# Revit family: CPS
name_source: partatom
category: Mechanical Equipment
units: mm (PartAtom-declared; Revit-internal decimal feet)

## family parameters
Always vertical = Yes
Cut with Voids When Loaded = No
Part Type = Normal
Room Calculation Point = No
Round Connector Dimension = Use Radius
Shared = No
Work Plane-Based = No

## types (33) — shared parameters
-.125 = -1/8"
-1.5 = -1 1/2"
0 = 0"
1.5 = 1 1/2"
CHECK = Yes
Manufacturer = Loren Cook Company
ONE EIGHTH = 1/8"
TA = 20"
TB = 3"
UNCHECK = No
URL = www.lorencook.com

## per-type parameters (varying)
- 135-CPS_CLASS_1: (C/2)-.25=8 9/16"; (C/2)-1.5=7 5/16"; -(A+.25)=-10 9/16"; A=10 5/16"; A+.25=10 9/16"; B=14 3/4"; C=17 5/8"; C/2=8 13/16"; C/8=2 15/16"; C/8*7=5 1/2"; CLASS=1"; CUT=2"; D=18"; E=26 11/16"; E-F=12 13/16"; F=13 7/8"; F-.125=13 3/4"; G=9 3/8"; G-V=1 3/8"; H=27"; J=13 1/2"; K=12"; L=13"; M=15 1/8"; Model=CPS_CLASS_1; N=12 1/8"; P=34 3/16"; P-D=16 3/16"; P-U=32 9/16"; Q=3"; R=1"; S=9/16"; S/2=9/32"; Stack Ht=88 1/8"; T=3/4"; Type Comments=Steel Flat Blade Centrifugal Blower Arrangement 10 Class 1; U=1 5/8"; U-.125=1 1/2"; V=8"; W=4"; W+1.5=5 1/2"; W+1.5+K+L=30 1/2"; W+M=19 1/8"; X=17 15/16"; Y=8 5/8"; Z=6"
- 150-CPS_CLASS_1: (C/2)-.25=9 5/16"; (C/2)-1.5=8 1/16"; -(A+.25)=-11 11/16"; A=11 7/16"; A+.25=11 11/16"; B=16 7/16"; C=19 1/8"; C/2=9 9/16"; C/8=3 3/16"; C/8*7=5 31/32"; CLASS=1"; CUT=2"; D=19 1/16"; E=29 9/16"; E-F=14 1/4"; F=15 5/16"; F-.125=15 3/16"; G=9 3/8"; G-V=1 3/8"; H=29 1/16"; J=14 5/8"; K=12"; L=14 1/8"; M=15 1/8"; Model=CPS_CLASS_1; N=13 1/4"; P=37 1/8"; P-D=18 1/16"; P-U=35 1/2"; Q=3"; R=1"; S=9/16"; S/2=9/32"; Stack Ht=85 5/8"; T=3/4"; Type Comments=Steel Flat Blade Centrifugal Blower Arrangement 10 Class 1; U=1 5/8"; U-.125=1 1/2"; V=8"; W=4"; W+1.5=5 1/2"; W+1.5+K+L=31 5/8"; W+M=19 1/8"; X=19 5/8"; Y=8 5/8"; Z=6 9/16"
- 165-CPS_CLASS_1: (C/2)-.25=10 11/32"; (C/2)-1.5=9 3/32"; -(A+.25)=-12 7/8"; A=12 5/8"; A+.25=12 7/8"; B=18 1/16"; C=21 3/16"; C/2=10 19/32"; C/8=3 17/32"; C/8*7=6 5/8"; CLASS=1"; CUT=2"; D=20 7/16"; E=32 1/16"; E-F=15 11/16"; F=16 3/8"; F-.125=16 1/4"; G=9 3/8"; G-V=1 3/8"; H=31 7/16"; J=15 13/16"; K=12"; L=15 5/16"; M=15 1/8"; Model=CPS_CLASS_1; N=14 7/16"; P=39 7/8"; P-D=19 7/16"; P-U=38 1/4"; Q=3"; R=1"; S=9/16"; S/2=9/32"; Stack Ht=83 3/16"; T=3/4"; Type Comments=Steel Flat Blade Centrifugal Blower Arrangement 10 Class 1; U=1 5/8"; U-.125=1 1/2"; V=8"; W=4"; W+1.5=5 1/2"; W+1.5+K+L=32 13/16"; W+M=19 1/8"; X=21 1/4"; Y=8 5/8"; Z=7 3/16"
- 180-CPS_CLASS_1: (C/2)-.25=11 3/32"; (C/2)-1.5=9 27/32"; -(A+.25)=-14"; A=13 3/4"; A+.25=14"; B=19 11/16"; C=22 11/16"; C/2=11 11/32"; C/8=3 25/32"; C/8*7=7 3/32"; CLASS=1"; CUT=2"; D=22 1/16"; E=34 3/4"; E-F=17 1/8"; F=17 5/8"; F-.125=17 1/2"; G=10 3/8"; G-V=1 3/8"; H=33 9/16"; J=16 15/16"; K=12"; L=16 7/16"; M=15 1/8"; Model=CPS_CLASS_1; N=15 9/16"; P=43 1/8"; P-D=21 1/16"; P-U=41 1/2"; Q=3"; R=1 3/16"; S=9/16"; S/2=9/32"; Stack Ht=80 5/16"; T=3/4"; Type Comments=Steel Flat Blade Centrifugal Blower Arrangement 10 Class 1; U=1 5/8"; U-.125=1 1/2"; V=9"; W=4"; W+1.5=5 1/2"; W+1.5+K+L=33 15/16"; W+M=19 1/8"; X=22 7/8"; Y=9 5/8"; Z=7 3/4"
- 195-CPS_CLASS_1: (C/2)-.25=11 27/32"; (C/2)-1.5=10 19/32"; -(A+.25)=-15 3/16"; A=14 15/16"; A+.25=15 3/16"; B=21 5/16"; C=24 3/16"; C/2=12 3/32"; C/8=4 1/32"; C/8*7=7 9/16"; CLASS=1"; CUT=2"; D=23 11/16"; E=36 5/16"; E-F=18 1/2"; F=17 13/16"; F-.125=17 11/16"; G=10 3/8"; G-V=1 3/8"; H=35 11/16"; J=18 3/16"; K=15"; L=17 5/8"; M=18 1/8"; Model=CPS_CLASS_1; N=16 3/4"; P=46 3/8"; P-D=22 11/16"; P-U=44 3/4"; Q=3"; R=1 3/16"; S=9/16"; S/2=9/32"; Stack Ht=78 1/2"; T=3/4"; Type Comments=Steel Flat Blade Centrifugal Blower Arrangement 10 Class 1; U=1 5/8"; U-.125=1 1/2"; V=9"; W=4"; W+1.5=5 1/2"; W+1.5+K+L=38 1/8"; W+M=22 1/8"; X=24 1/2"; Y=9 5/8"; Z=8 5/16"
- 210-CPS_CLASS_1: (C/2)-.25=12 23/32"; (C/2)-1.5=11 15/32"; -(A+.25)=-16 5/16"; A=16 1/16"; A+.25=16 5/16"; B=23"; C=25 15/16"; C/2=12 31/32"; C/8=4 5/16"; C/8*7=8 3/32"; CLASS=1"; CUT=2"; D=25 3/8"; E=39 15/16"; E-F=19 15/16"; F=20"; F-.125=19 7/8"; G=11 3/8"; G-V=1 3/8"; H=38 7/8"; J=19 5/16"; K=15"; L=18 3/4"; M=18 1/8"; Model=CPS_CLASS_1; N=17 7/8"; P=49 3/4"; P-D=24 3/8"; P-U=48 1/8"; Q=4"; R=1 7/16"; S=9/16"; S/2=9/32"; Stack Ht=74 5/8"; T=3/4"; Type Comments=Steel Flat Blade Centrifugal Blower Arrangement 10 Class 1; U=1 5/8"; U-.125=1 1/2"; V=10"; W=5"; W+1.5=6 1/2"; W+1.5+K+L=40 1/4"; W+M=23 1/8"; X=26 3/16"; Y=10 5/8"; Z=8 7/8"
- 225-CPS_CLASS_1: (C/2)-.25=13 15/32"; (C/2)-1.5=12 7/32"; -(A+.25)=-17 7/16"; A=17 3/16"; A+.25=17 7/16"; B=24 5/8"; C=27 7/16"; C/2=13 23/32"; C/8=4 9/16"; C/8*7=8 9/16"; CLASS=1"; CUT=2"; D=27"; E=42"; E-F=21 3/8"; F=20 5/8"; F-.125=20 1/2"; G=11 7/8"; G-V=1 3/8"; H=41"; J=20 7/16"; K=15"; L=19 7/8"; M=18 1/8"; Model=CPS_CLASS_1; N=19"; P=53"; P-D=26"; P-U=51 3/8"; Q=4"; R=1 7/16"; S=9/16"; S/2=9/32"; Stack Ht=72 3/8"; T=3/4"; Type Comments=Steel Flat Blade Centrifugal Blower Arrangement 10 Class 1; U=1 5/8"; U-.125=1 1/2"; V=10 1/2"; W=5"; W+1.5=6 1/2"; W+1.5+K+L=41 3/8"; W+M=23 1/8"; X=27 13/16"; Y=11 1/8"; Z=9 7/16"
- 245-CPS_CLASS_1: (C/2)-.25=14 15/32"; (C/2)-1.5=13 7/32"; -(A+.25)=-19"; A=18 3/4"; A+.25=19"; B=26 13/16"; C=29 7/16"; C/2=14 23/32"; C/8=4 29/32"; C/8*7=9 3/16"; CLASS=1"; CUT=2"; D=29 5/8"; E=45 1/16"; E-F=23 5/16"; F=21 3/4"; F-.125=21 5/8"; G=13 3/8"; G-V=1 7/8"; H=44 5/8"; J=23"; K=15"; L=21 11/16"; M=18 1/8"; Model=CPS_CLASS_1; N=21 1/16"; P=58 1/4"; P-D=28 5/8"; P-U=56 1/8"; Q=4"; R=1 11/16"; S=11/16"; S/2=11/32"; Stack Ht=68 5/8"; T=1"; Type Comments=Steel Flat Blade Centrifugal Blower Arrangement 10 Class 1; U=2 1/8"; U-.125=2"; V=11 1/2"; W=5"; W+1.5=6 1/2"; W+1.5+K+L=43 3/16"; W+M=23 1/8"; X=31"; Y=12 3/8"; Z=10 1/2"
- 270-CPS_CLASS_1: (C/2)-.25=15 23/32"; (C/2)-1.5=14 15/32"; -(A+.25)=-20 7/8"; A=20 5/8"; A+.25=20 7/8"; B=29 9/16"; C=31 15/16"; C/2=15 31/32"; C/8=5 5/16"; C/8*7=9 31/32"; CLASS=1"; CUT=2 1/4"; D=32 3/8"; E=49 1/16"; E-F=25 11/16"; F=23 3/8"; F-.125=23 1/4"; G=14 3/8"; G-V=1 7/8"; H=48 7/8"; J=24 7/8"; K=18"; L=23 9/16"; M=21 1/8"; Model=CPS_CLASS_1; N=22 15/16"; P=63 3/4"; P-D=31 3/8"; P-U=61 5/8"; Q=4"; R=1 11/16"; S=11/16"; S/2=11/32"; Stack Ht=64 1/4"; T=1"; Type Comments=Steel Flat Blade Centrifugal Blower Arrangement 10 Class 1; U=2 1/8"; U-.125=2"; V=12 1/2"; W=5"; W+1.5=6 1/2"; W+1.5+K+L=48 1/16"; W+M=26 1/8"; X=33 3/4"; Y=13 3/8"; Z=11 7/16"
- 300-CPS_CLASS_1: (C/2)-.25=17 7/32"; (C/2)-1.5=15 31/32"; -(A+.25)=-23 3/16"; A=22 15/16"; A+.25=23 3/16"; B=32 13/16"; C=34 15/16"; C/2=17 15/32"; C/8=5 13/16"; C/8*7=10 29/32"; CLASS=1"; CUT=2 1/2"; D=35 5/8"; E=54 3/8"; E-F=28 1/2"; F=25 7/8"; F-.125=25 3/4"; G=15 5/16"; G-V=1 13/16"; H=53 5/8"; J=27 3/16"; K=18"; L=26"; M=21 3/16"; Model=CPS_CLASS_1; N=25 5/16"; P=71 1/4"; P-D=35 5/8"; P-U=69 1/8"; Q=4"; R=1 15/16"; S=11/16"; S/2=11/32"; Stack Ht=58 1/2"; T=1"; Type Comments=Steel Flat Blade Centrifugal Blower Arrangement 10 Class 1; U=2 1/8"; U-.125=2"; V=13 1/2"; W=5"; W+1.5=6 1/2"; W+1.5+K+L=50 1/2"; W+M=26 3/16"; X=37"; Y=14 5/16"; Z=12 5/8"
- 330-CPS_CLASS_1: (C/2)-.25=18 23/32"; (C/2)-1.5=17 15/32"; -(A+.25)=-25 1/2"; A=25 1/4"; A+.25=25 1/2"; B=36 1/8"; C=37 15/16"; C/2=18 31/32"; C/8=6 5/16"; C/8*7=11 27/32"; CLASS=1"; CUT=2 3/4"; D=38 7/8"; E=59 13/16"; E-F=31 3/8"; F=28 7/16"; F-.125=28 5/16"; G=16 13/16"; G-V=1 13/16"; H=58 3/8"; J=29 7/16"; K=18"; L=28 5/16"; M=21 3/16"; Model=CPS_CLASS_1; N=27 5/8"; P=76 3/4"; P-D=37 7/8"; P-U=74 5/8"; Q=4"; R=1 15/16"; S=13/16"; S/2=13/32"; Stack Ht=52 11/16"; T=1"; Type Comments=Steel Flat Blade Centrifugal Blower Arrangement 10 Class 1; U=2 1/8"; U-.125=2"; V=15"; W=5"; W+1.5=6 1/2"; W+1.5+K+L=52 13/16"; W+M=26 3/16"; X=40 5/16"; Y=15 13/16"; Z=13 3/4"
- 365-CPS_CLASS_1: (C/2)-.25=20 15/32"; (C/2)-1.5=19 7/32"; -(A+.25)=-28 1/8"; A=27 7/8"; A+.25=28 1/8"; B=39 15/16"; C=41 7/16"; C/2=20 23/32"; C/8=6 29/32"; C/8*7=12 15/16"; CLASS=1"; CUT=3"; D=42 3/4"; E=66 1/8"; E-F=34 11/16"; F=31 7/16"; F-.125=31 5/16"; G=17 13/16"; G-V=1 13/16"; H=64 1/4"; J=32 1/16"; K=21"; L=30 15/16"; M=24 3/16"; Model=CPS_CLASS_1; N=30 1/4"; P=84 1/2"; P-D=41 3/4"; P-U=82 3/8"; Q=5"; R=2 3/16"; S=13/16"; S/2=13/32"; Stack Ht=45 13/16"; T=1"; Type Comments=Steel Flat Blade Centrifugal Blower Arrangement 10 Class 1; U=2 1/8"; U-.125=2"; V=16"; W=6"; W+1.5=7 1/2"; W+1.5+K+L=59 7/16"; W+M=30 3/16"; X=44 3/16"; Y=16 13/16"; Z=15 1/16"
- 402-CPS_CLASS_1: (C/2)-.25=22 11/32"; (C/2)-1.5=21 3/32"; -(A+.25)=-31"; A=30 3/4"; A+.25=31"; B=44 1/16"; C=45 3/16"; C/2=22 19/32"; C/8=7 17/32"; C/8*7=14 1/8"; CLASS=1"; CUT=3 1/4"; D=46 3/4"; E=72 15/16"; E-F=38 1/4"; F=34 11/16"; F-.125=34 9/16"; G=19 13/16"; G-V=1 13/16"; H=70 1/4"; J=34 15/16"; K=21"; L=34 5/16"; M=24 3/16"; Model=CPS_CLASS_1; N=34 1/8"; P=92 1/2"; P-D=45 3/4"; P-U=90 3/8"; Q=5"; R=2 3/16"; S=13/16"; S/2=13/32"; Stack Ht=38 9/16"; T=1"; Type Comments=Steel Flat Blade Centrifugal Blower Arrangement 10 Class 1; U=2 1/8"; U-.125=2"; V=18"; W=6"; W+1.5=7 1/2"; W+1.5+K+L=62 13/16"; W+M=30 3/16"; X=48 5/16"; Y=18 13/16"; Z=17"
- 445-CPS_CLASS_1: (C/2)-.25=24 15/32"; (C/2)-1.5=23 7/32"; -(A+.25)=-34 1/4"; A=34"; A+.25=34 1/4"; B=48 11/16"; C=49 7/16"; C/2=24 23/32"; C/8=8 1/4"; C/8*7=15 7/16"; CLASS=1"; CUT=3 1/2"; D=51 3/8"; E=80 9/16"; E-F=42 1/4"; F=38 5/16"; F-.125=38 3/16"; G=21 13/16"; G-V=1 13/16"; H=76 7/8"; J=38 3/16"; K=25"; L=37 9/16"; M=28 3/16"; Model=CPS_CLASS_1; N=37 3/8"; P=101 3/4"; P-D=50 3/8"; P-U=99 5/8"; Q=5"; R=2 7/16"; S=13/16"; S/2=13/32"; Stack Ht=30 5/16"; T=1"; Type Comments=Steel Flat Blade Centrifugal Blower Arrangement 10 Class 1; U=2 1/8"; U-.125=2"; V=20"; W=6"; W+1.5=7 1/2"; W+1.5+K+L=70 1/16"; W+M=34 3/16"; X=52 15/16"; Y=20 13/16"; Z=18 5/8"
- 490-CPS_CLASS_1: (C/2)-.25=27 1/4"; (C/2)-1.5=26"; -(A+.25)=-37 7/16"; A=37 3/16"; A+.25=37 7/16"; B=53 5/8"; C=55"; C/2=27 1/2"; C/8=9 5/32"; C/8*7=17 3/16"; CLASS=1"; CUT=4"; D=56 1/4"; E=88 3/4"; E-F=46 9/16"; F=42 3/16"; F-.125=42 1/16"; G=23 13/16"; G-V=1 13/16"; H=84 1/4"; J=41 5/8"; K=25"; L=41"; M=28 3/16"; Model=CPS_CLASS_1; N=40 3/16"; P=111 1/2"; P-D=55 1/4"; P-U=109 3/8"; Q=5"; R=2 7/16"; S=13/16"; S/2=13/32"; Stack Ht=21 9/16"; T=1"; Type Comments=Steel Flat Blade Centrifugal Blower Arrangement 10 Class 1; U=2 1/8"; U-.125=2"; V=22"; W=6"; W+1.5=7 1/2"; W+1.5+K+L=73 1/2"; W+M=34 3/16"; X=57 7/8"; Y=22 13/16"; Z=20 3/8"
- 120-CPS_CLASS_1: (C/2)-.25=7 13/16"; (C/2)-1.5=6 9/16"; -(A+.25)=-9 7/16"; A=9 3/16"; A+.25=9 7/16"; B=13 1/8"; C=16 1/8"; C/2=8 1/16"; C/8=2 11/16"; C/8*7=5 1/32"; CLASS=1"; CUT=2 1/2"; D=18"; E=24 13/16"; E-F=11 7/16"; F=13 3/8"; F-.125=13 1/4"; G=9 3/8"; G-V=1 3/8"; H=26 1/4"; J=12 3/8"; K=10"; L=11 7/8"; M=13 1/8"; Model=CPS_CLASS_1; N=11"; P=32 9/16"; P-D=14 9/16"; P-U=30 15/16"; Q=3"; R=1"; S=9/16"; S/2=9/32"; Stack Ht=88 5/8"; T=3/4"; Type Comments=Steel Flat Blade Centrifugal Blower Arrangement 10 Class 1; U=1 5/8"; U-.125=1 1/2"; V=8"; W=4"; W+1.5=5 1/2"; W+1.5+K+L=27 3/8"; W+M=17 1/8"; X=16 5/16"; Y=8 5/8"; Z=5 7/16"
- 100-CPS_CLASS_1: (C/2)-.25=6 13/16"; (C/2)-1.5=5 9/16"; -(A+.25)=-7 13/16"; A=7 9/16"; A+.25=7 13/16"; B=10 15/16"; C=14 1/8"; C/2=7 1/16"; C/8=2 11/32"; C/8*7=4 13/32"; CLASS=1"; CUT=3 1/2"; D=18"; E=22 1/4"; E-F=9 1/2"; F=12 3/4"; F-.125=12 5/8"; G=9 3/8"; G-V=1 3/8"; H=25 1/4"; J=10 3/4"; K=10"; L=10 1/4"; M=13 1/8"; Model=CPS_CLASS_1; N=9 3/8"; P=30 3/8"; P-D=12 3/8"; P-U=28 3/4"; Q=3"; R=1"; S=9/16"; S/2=9/32"; Stack Ht=89 1/4"; T=3/4"; Type Comments=Steel Flat Blade Centrifugal Blower Arrangement 10 Class 1; U=1 5/8"; U-.125=1 1/2"; V=8"; W=4"; W+1.5=5 1/2"; W+1.5+K+L=25 3/4"; W+M=17 1/8"; X=14 1/16"; Y=8 5/8"; Z=4 5/8"
- 120-CPS_CLASS_2: (C/2)-.25=7 13/16"; (C/2)-1.5=6 9/16"; -(A+.25)=-9 7/16"; A=9 3/16"; A+.25=9 7/16"; B=13 1/8"; C=16 1/8"; C/2=8 1/16"; C/8=2 11/16"; C/8*7=5 1/32"; CLASS=2"; CUT=2 1/2"; D=22"; E=24 7/8"; E-F=11 1/2"; F=13 3/8"; F-.125=13 1/4"; G=10 3/8"; G-V=1 3/8"; H=30 1/4"; J=12 3/8"; K=18"; L=12 5/16"; M=21 1/8"; Model=CPS_CLASS_2; N=11 1/4"; P=36 5/8"; P-D=14 5/8"; P-U=35"; Q=3"; R=1 7/16"; S=9/16"; S/2=9/32"; Stack Ht=84 5/8"; T=3/4"; Type Comments=Steel Flat Blade Centrifugal Blower Arrangement 10 Class 2; U=1 5/8"; U-.125=1 1/2"; V=9"; W=4"; W+1.5=5 1/2"; W+1.5+K+L=35 13/16"; W+M=25 1/8"; X=16 5/16"; Y=9 5/8"; Z=5 9/16"
- 135-CPS_CLASS_2: (C/2)-.25=8 9/16"; (C/2)-1.5=7 5/16"; -(A+.25)=-10 9/16"; A=10 5/16"; A+.25=10 9/16"; B=14 5/8"; C=17 5/8"; C/2=8 13/16"; C/8=2 15/16"; C/8*7=5 1/2"; CLASS=2"; CUT=2"; D=22"; E=26 3/4"; E-F=12 7/8"; F=13 7/8"; F-.125=13 3/4"; G=10 3/8"; G-V=1 3/8"; H=31"; J=13 1/2"; K=18"; L=13 7/16"; M=21 1/8"; Model=CPS_CLASS_2; N=12 3/8"; P=38 1/4"; P-D=16 1/4"; P-U=36 5/8"; Q=3"; R=1 7/16"; S=9/16"; S/2=9/32"; Stack Ht=84 1/8"; T=3/4"; Type Comments=Steel Flat Blade Centrifugal Blower Arrangement 10 Class 2; U=1 5/8"; U-.125=1 1/2"; V=9"; W=4"; W+1.5=5 1/2"; W+1.5+K+L=36 15/16"; W+M=25 1/8"; X=17 15/16"; Y=9 5/8"; Z=6 1/8"
- 150-CPS_CLASS_2: (C/2)-.25=9 5/16"; (C/2)-1.5=8 1/16"; -(A+.25)=-11 11/16"; A=11 7/16"; A+.25=11 11/16"; B=16 7/16"; C=19 1/8"; C/2=9 9/16"; C/8=3 3/16"; C/8*7=5 31/32"; CLASS=2"; CUT=2"; D=22"; E=29 5/8"; E-F=14 5/16"; F=15 5/16"; F-.125=15 3/16"; G=10 7/8"; G-V=1 3/8"; H=32"; J=14 5/8"; K=18"; L=15 15/32"; M=21 1/8"; Model=CPS_CLASS_2; N=13 1/2"; P=39 7/8"; P-D=17 7/8"; P-U=38 1/4"; Q=3"; R=1 7/16"; S=9/16"; S/2=9/32"; Stack Ht=82 11/16"; T=3/4"; Type Comments=Steel Flat Blade Centrifugal Blower Arrangement 10 Class 2; U=1 5/8"; U-.125=1 1/2"; V=9 1/2"; W=4"; W+1.5=5 1/2"; W+1.5+K+L=38 31/32"; W+M=25 1/8"; X=19 5/8"; Y=10 1/8"; Z=6 11/16"
- 165-CPS_CLASS_2: (C/2)-.25=10 11/32"; (C/2)-1.5=9 3/32"; -(A+.25)=-12 7/8"; A=12 5/8"; A+.25=12 7/8"; B=18 1/16"; C=21 3/16"; C/2=10 19/32"; C/8=3 17/32"; C/8*7=6 5/8"; CLASS=2"; CUT=2"; D=24"; E=32 1/8"; E-F=15 3/4"; F=16 3/8"; F-.125=16 1/4"; G=13"; G-V=1 3/4"; H=35"; J=15 13/16"; K=22 1/8"; L=16 1/8"; M=25 1/4"; Model=CPS_CLASS_2; N=15 1/16"; P=43 1/2"; P-D=19 1/2"; P-U=41 7/8"; Q=3"; R=1 7/16"; S=9/16"; S/2=9/32"; Stack Ht=79 5/8"; T=3/4"; Type Comments=Steel Flat Blade Centrifugal Blower Arrangement 10 Class 2; U=1 5/8"; U-.125=1 1/2"; V=11 1/4"; W=4"; W+1.5=5 1/2"; W+1.5+K+L=43 3/4"; W+M=29 1/4"; X=21 1/4"; Y=12 1/4"; Z=7 5/8"
- 180-CPS_CLASS_2: (C/2)-.25=11 3/32"; (C/2)-1.5=9 27/32"; -(A+.25)=-14"; A=13 3/4"; A+.25=14"; B=19 11/16"; C=22 11/16"; C/2=11 11/32"; C/8=3 25/32"; C/8*7=7 3/32"; CLASS=2"; CUT=2"; D=24"; E=34 13/16"; E-F=17 3/16"; F=17 5/8"; F-.125=17 1/2"; G=13"; G-V=1 3/4"; H=35 1/2"; J=16 15/16"; K=22 1/8"; L=17 1/4"; M=25 1/4"; Model=CPS_CLASS_2; N=16 3/16"; P=45 1/8"; P-D=21 1/8"; P-U=43 1/2"; Q=3"; R=1 11/16"; S=9/16"; S/2=9/32"; Stack Ht=78 3/8"; T=3/4"; Type Comments=Steel Flat Blade Centrifugal Blower Arrangement 10 Class 2; U=1 5/8"; U-.125=1 1/2"; V=11 1/4"; W=4"; W+1.5=5 1/2"; W+1.5+K+L=44 7/8"; W+M=29 1/4"; X=22 7/8"; Y=12 1/4"; Z=8 3/16"
- 195-CPS_CLASS_2: (C/2)-.25=11 27/32"; (C/2)-1.5=10 19/32"; -(A+.25)=-15 3/16"; A=14 15/16"; A+.25=15 3/16"; B=21 5/16"; C=24 3/16"; C/2=12 3/32"; C/8=4 1/32"; C/8*7=7 9/16"; CLASS=2"; CUT=2"; D=24 1/4"; E=36 3/8"; E-F=18 9/16"; F=17 13/16"; F-.125=17 11/16"; G=13 3/4"; G-V=1 3/4"; H=36 1/4"; J=18 3/16"; K=22 1/8"; L=18 1/2"; M=25 1/4"; Model=CPS_CLASS_2; N=17 3/8"; P=47"; P-D=22 3/4"; P-U=45 3/8"; Q=3"; R=1 11/16"; S=9/16"; S/2=9/32"; Stack Ht=77 15/16"; T=3/4"; Type Comments=Steel Flat Blade Centrifugal Blower Arrangement 10 Class 2; U=1 5/8"; U-.125=1 1/2"; V=12"; W=4"; W+1.5=5 1/2"; W+1.5+K+L=46 1/8"; W+M=29 1/4"; X=24 1/2"; Y=13"; Z=8 13/16"
- 210-CPS_CLASS_2: (C/2)-.25=12 23/32"; (C/2)-1.5=11 15/32"; -(A+.25)=-16 5/16"; A=16 1/16"; A+.25=16 5/16"; B=23"; C=25 15/16"; C/2=12 31/32"; C/8=4 5/16"; C/8*7=8 3/32"; CLASS=2"; CUT=2"; D=25 3/8"; E=40"; E-F=20"; F=20"; F-.125=19 7/8"; G=13 3/4"; G-V=1 3/4"; H=39"; J=19 5/16"; K=22 1/8"; L=19 5/8"; M=25 1/4"; Model=CPS_CLASS_2; N=18 1/2"; P=49 13/16"; P-D=24 7/16"; P-U=48 3/16"; Q=4"; R=1 11/16"; S=9/16"; S/2=9/32"; Stack Ht=74 5/8"; T=3/4"; Type Comments=Steel Flat Blade Centrifugal Blower Arrangement 10 Class 2; U=1 5/8"; U-.125=1 1/2"; V=12"; W=5"; W+1.5=6 1/2"; W+1.5+K+L=48 1/4"; W+M=30 1/4"; X=26 3/16"; Y=13"; Z=9 3/8"
- 225-CPS_CLASS_2: (C/2)-.25=13 15/32"; (C/2)-1.5=12 7/32"; -(A+.25)=-17 7/16"; A=17 3/16"; A+.25=17 7/16"; B=24 5/8"; C=27 7/16"; C/2=13 23/32"; C/8=4 9/16"; C/8*7=8 9/16"; CLASS=2"; CUT=2"; D=27"; E=42 1/16"; E-F=21 7/16"; F=20 5/8"; F-.125=20 1/2"; G=13 7/8"; G-V=1 13/16"; H=41"; J=20 7/16"; K=22 1/8"; L=20 7/8"; M=25 1/4"; Model=CPS_CLASS_2; N=19 3/4"; P=53 3/16"; P-D=26 3/16"; P-U=51 9/16"; Q=4"; R=1 11/16"; S=9/16"; S/2=9/32"; Stack Ht=72 3/8"; T=3/4"; Type Comments=Steel Flat Blade Centrifugal Blower Arrangement 10 Class 2; U=1 5/8"; U-.125=1 1/2"; V=12 1/16"; W=5"; W+1.5=6 1/2"; W+1.5+K+L=49 1/2"; W+M=30 1/4"; X=27 13/16"; Y=13 1/8"; Z=10 1/16"
- 245-CPS_CLASS_2: (C/2)-.25=14 15/32"; (C/2)-1.5=13 7/32"; -(A+.25)=-19"; A=18 3/4"; A+.25=19"; B=26 13/16"; C=29 7/16"; C/2=14 23/32"; C/8=4 29/32"; C/8*7=9 3/16"; CLASS=2"; CUT=2"; D=29 5/8"; E=45 1/8"; E-F=23 3/8"; F=21 3/4"; F-.125=21 5/8"; G=14 15/16"; G-V=1 13/16"; H=44 5/8"; J=23"; K=24 1/8"; L=22 5/16"; M=27 5/16"; Model=CPS_CLASS_2; N=21 5/16"; P=58 5/16"; P-D=28 11/16"; P-U=56 3/16"; Q=4"; R=1 15/16"; S=11/16"; S/2=11/32"; Stack Ht=68 5/8"; T=1"; Type Comments=Steel Flat Blade Centrifugal Blower Arrangement 10 Class 2; U=2 1/8"; U-.125=2"; V=13 1/8"; W=5"; W+1.5=6 1/2"; W+1.5+K+L=52 15/16"; W+M=32 5/16"; X=31"; Y=13 15/16"; Z=10 5/8"
- 270-CPS_CLASS_2: (C/2)-.25=15 23/32"; (C/2)-1.5=14 15/32"; -(A+.25)=-20 7/8"; A=20 5/8"; A+.25=20 7/8"; B=29 9/16"; C=31 15/16"; C/2=15 31/32"; C/8=5 5/16"; C/8*7=9 31/32"; CLASS=2"; CUT=2 1/4"; D=32 3/8"; E=49 1/8"; E-F=25 3/4"; F=23 3/8"; F-.125=23 1/4"; G=15 7/16"; G-V=2 5/16"; H=48 7/8"; J=24 7/8"; K=24 1/8"; L=24 11/16"; M=27 5/16"; Model=CPS_CLASS_2; N=23 11/16"; P=63 13/16"; P-D=31 7/16"; P-U=61 11/16"; Q=4"; R=1 15/16"; S=11/16"; S/2=11/32"; Stack Ht=64 1/4"; T=1"; Type Comments=Steel Flat Blade Centrifugal Blower Arrangement 10 Class 2; U=2 1/8"; U-.125=2"; V=13 1/8"; W=5"; W+1.5=6 1/2"; W+1.5+K+L=55 5/16"; W+M=32 5/16"; X=33 3/4"; Y=14 7/16"; Z=12 1/16"
- 300-CPS_CLASS_2: (C/2)-.25=17 7/32"; (C/2)-1.5=15 31/32"; -(A+.25)=-23 3/16"; A=22 15/16"; A+.25=23 3/16"; B=32 13/16"; C=34 15/16"; C/2=17 15/32"; C/8=5 13/16"; C/8*7=10 29/32"; CLASS=2"; CUT=2 1/2"; D=35 5/8"; E=54 1/2"; E-F=28 5/8"; F=25 7/8"; F-.125=25 3/4"; G=16 1/16"; G-V=2 3/8"; H=53 5/8"; J=27 3/16"; K=26"; L=27 3/16"; M=29 3/16"; Model=CPS_CLASS_2; N=26 3/16"; P=70 3/8"; P-D=34 3/4"; P-U=68 1/4"; Q=4"; R=2 3/16"; S=11/16"; S/2=11/32"; Stack Ht=58 1/2"; T=1"; Type Comments=Steel Flat Blade Centrifugal Blower Arrangement 10 Class 2; U=2 1/8"; U-.125=2"; V=13 11/16"; W=5"; W+1.5=6 1/2"; W+1.5+K+L=59 11/16"; W+M=34 3/16"; X=37"; Y=15 1/16"; Z=13 5/16"
- 330-CPS_CLASS_2: (C/2)-.25=18 23/32"; (C/2)-1.5=17 15/32"; -(A+.25)=-25 1/2"; A=25 1/4"; A+.25=25 1/2"; B=36 1/8"; C=37 15/16"; C/2=18 31/32"; C/8=6 5/16"; C/8*7=11 27/32"; CLASS=2"; CUT=2 3/4"; D=38 7/8"; E=59 15/16"; E-F=31 1/2"; F=28 7/16"; F-.125=28 5/16"; G=17 5/8"; G-V=2 3/8"; H=58 3/8"; J=29 7/16"; K=26"; L=29 9/16"; M=29 3/16"; Model=CPS_CLASS_2; N=28 9/16"; P=76 7/8"; P-D=38"; P-U=74 3/4"; Q=4"; R=2 3/16"; S=13/16"; S/2=13/32"; Stack Ht=52 11/16"; T=1"; Type Comments=Steel Flat Blade Centrifugal Blower Arrangement 10 Class 2; U=2 1/8"; U-.125=2"; V=15 1/4"; W=5"; W+1.5=6 1/2"; W+1.5+K+L=62 1/16"; W+M=34 3/16"; X=40 5/16"; Y=16 5/8"; Z=14 9/16"
- 365-CPS_CLASS_2: (C/2)-.25=20 15/32"; (C/2)-1.5=19 7/32"; -(A+.25)=-28 1/8"; A=27 7/8"; A+.25=28 1/8"; B=39 15/16"; C=41 7/16"; C/2=20 23/32"; C/8=6 29/32"; C/8*7=12 15/16"; CLASS=2"; CUT=3"; D=42 3/4"; E=66 3/16"; E-F=34 3/4"; F=31 7/16"; F-.125=31 5/16"; G=18 13/16"; G-V=2 5/8"; H=64 1/4"; J=32 1/16"; K=26"; L=32 9/16"; M=29 1/4"; Model=CPS_CLASS_2; N=31 7/16"; P=84 1/2"; P-D=41 3/4"; P-U=82 3/8"; Q=5"; R=2 7/16"; S=13/16"; S/2=13/32"; Stack Ht=45 13/16"; T=1"; Type Comments=Steel Flat Blade Centrifugal Blower Arrangement 10 Class 2; U=2 1/8"; U-.125=2"; V=16 3/16"; W=6"; W+1.5=7 1/2"; W+1.5+K+L=66 1/16"; W+M=35 1/4"; X=44 3/16"; Y=17 13/16"; Z=16 1/8"
- 60-CPS_CLASS_1: (C/2)-.25=6 13/16"; (C/2)-1.5=5 9/16"; -(A+.25)=-7 13/16"; A=7 9/16"; A+.25=7 13/16"; B=10 15/16"; C=14 1/8"; C/2=7 1/16"; C/8=2 11/32"; C/8*7=4 13/32"; CLASS=1"; CUT=3 1/2"; D=18"; E=22 1/4"; E-F=9 1/2"; F=12 3/4"; F-.125=12 5/8"; G=9 3/8"; G-V=1 3/8"; H=25 1/4"; J=10 3/4"; K=10"; L=10 1/4"; M=13 1/8"; Model=CPS_CLASS_1; N=9 3/8"; P=30 3/8"; P-D=12 3/8"; P-U=28 3/4"; Q=3"; R=1"; S=9/16"; S/2=9/32"; Stack Ht=89 1/4"; T=3/4"; Type Comments=Steel Flat Blade Centrifugal Blower Arrangement 10 Class 1; U=1 5/8"; U-.125=1 1/2"; V=8"; W=4"; W+1.5=5 1/2"; W+1.5+K+L=25 3/4"; W+M=17 1/8"; X=14 1/16"; Y=8 5/8"; Z=4 5/8"
- 70-CPS_CLASS_1: (C/2)-.25=6 13/16"; (C/2)-1.5=5 9/16"; -(A+.25)=-7 13/16"; A=7 9/16"; A+.25=7 13/16"; B=10 15/16"; C=14 1/8"; C/2=7 1/16"; C/8=2 11/32"; C/8*7=4 13/32"; CLASS=1"; CUT=3 1/2"; D=18"; E=22 1/4"; E-F=9 1/2"; F=12 3/4"; F-.125=12 5/8"; G=9 3/8"; G-V=1 3/8"; H=25 1/4"; J=10 3/4"; K=10"; L=10 1/4"; M=13 1/8"; Model=CPS_CLASS_1; N=9 3/8"; P=30 3/8"; P-D=12 3/8"; P-U=28 3/4"; Q=3"; R=1"; S=9/16"; S/2=9/32"; Stack Ht=89 1/4"; T=3/4"; Type Comments=Steel Flat Blade Centrifugal Blower Arrangement 10 Class 1; U=1 5/8"; U-.125=1 1/2"; V=8"; W=4"; W+1.5=5 1/2"; W+1.5+K+L=25 3/4"; W+M=17 1/8"; X=14 1/16"; Y=8 5/8"; Z=4 5/8"
- 80-CPS_CLASS_1: (C/2)-.25=6 13/16"; (C/2)-1.5=5 9/16"; -(A+.25)=-7 13/16"; A=7 9/16"; A+.25=7 13/16"; B=10 15/16"; C=14 1/8"; C/2=7 1/16"; C/8=2 11/32"; C/8*7=4 13/32"; CLASS=1"; CUT=3 1/2"; D=18"; E=22 1/4"; E-F=9 1/2"; F=12 3/4"; F-.125=12 5/8"; G=9 3/8"; G-V=1 3/8"; H=25 1/4"; J=10 3/4"; K=10"; L=10 1/4"; M=13 1/8"; Model=CPS_CLASS_1; N=9 3/8"; P=30 3/8"; P-D=12 3/8"; P-U=28 3/4"; Q=3"; R=1"; S=9/16"; S/2=9/32"; Stack Ht=89 1/4"; T=3/4"; Type Comments=Steel Flat Blade Centrifugal Blower Arrangement 10 Class 1; U=1 5/8"; U-.125=1 1/2"; V=8"; W=4"; W+1.5=5 1/2"; W+1.5+K+L=25 3/4"; W+M=17 1/8"; X=14 1/16"; Y=8 5/8"; Z=4 5/8"

## geometry (parser evidence)
native form markers: Extrusion x1, Sweep x5
no freeform markers — native parametric forms only
